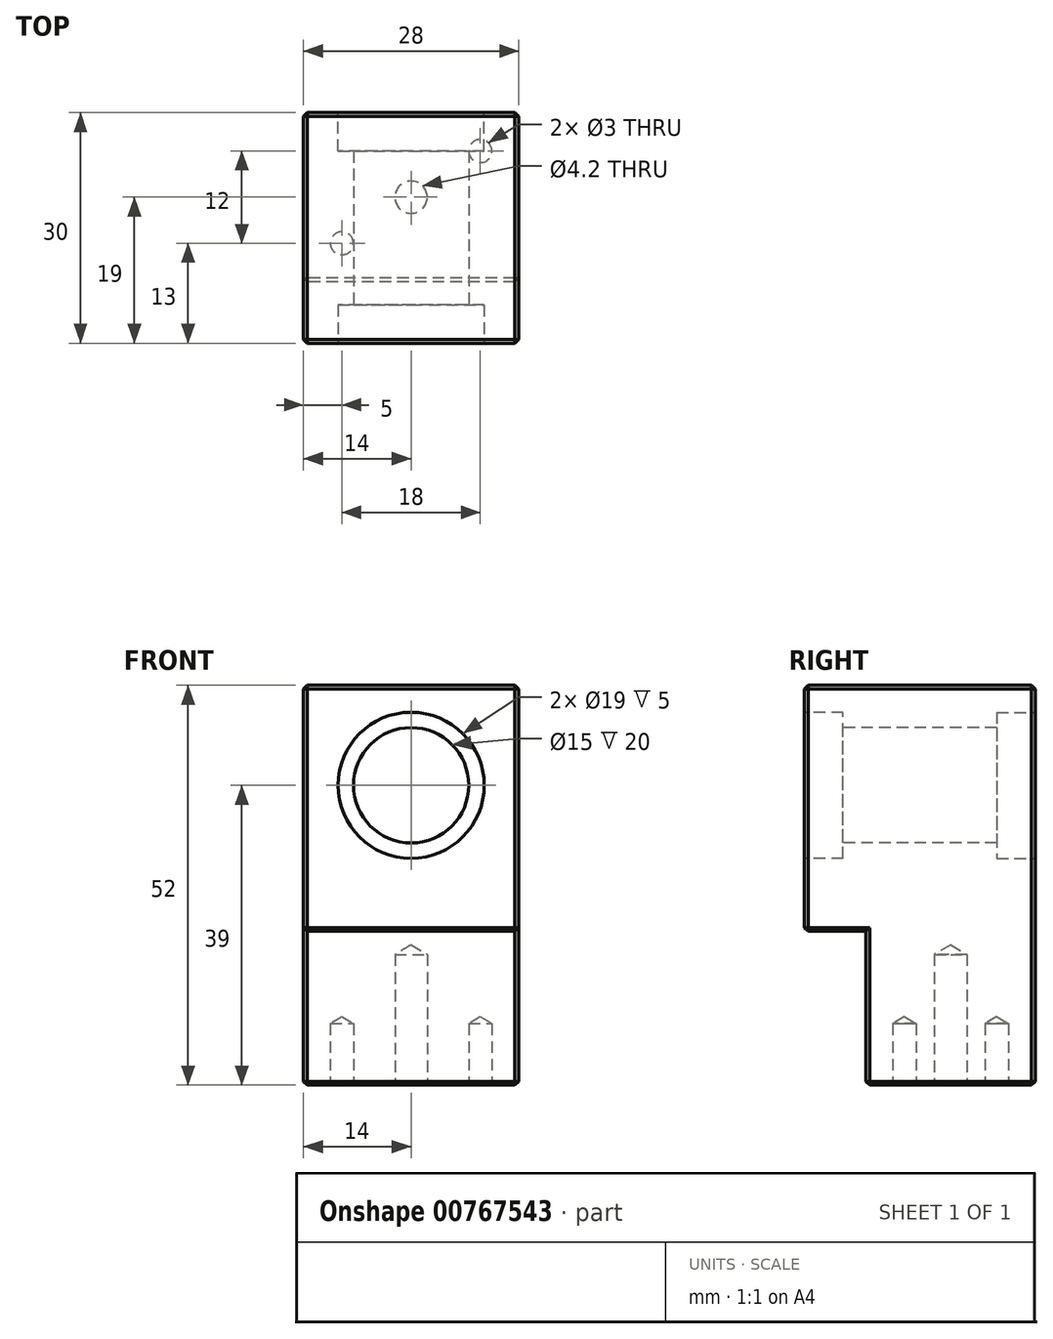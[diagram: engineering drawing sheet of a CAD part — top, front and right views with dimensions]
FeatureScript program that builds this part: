
annotation { "Feature Type Name" : "Feature", "Feature Type Description" : "" }
export const myFeature = defineFeature(function(context is Context, id is Id, definition is map)
    precondition{}
    {
        {
            var Q0;
            Q0=qCreatedBy(makeId("Right.planeOp"),FACE);
            var sketch = newSketch(context, id + "F0", { "sketchPlane" : qUnion([Q0])});
            skLineSegment(sketch, "E0", {"start": v(0, 0) * mm, "end": v(0, 20) * mm});
            skLineSegment(sketch, "E1", {"start": v(0, 20) * mm, "end": v(-8, 20) * mm});
            skLineSegment(sketch, "E2", {"start": v(-8, 20) * mm, "end": v(-8, 52) * mm});
            skLineSegment(sketch, "E3", {"start": v(-8, 52) * mm, "end": v(22, 52) * mm});
            skLineSegment(sketch, "E4", {"start": v(22, 52) * mm, "end": v(22, 0) * mm});
            skLineSegment(sketch, "E5", {"start": v(22, 0) * mm, "end": v(0, 0) * mm});
            skSolve(sketch);
        }
        {
            var Q0;
            Q0 = qSketchRegion(id + "F0", true);
            extrude(context, id + "F1", {"entities" : qUnion([Q0]), "endBound" : BoundingType.SYMMETRIC, "depth" : 28 * mm, "offsetDistance" : 25 * mm});
        }
        {
            var Q0;
            Q0=makeQuery(id+"F1.opExtrude","CAP_FACE",FACE,{"disambiguationData":[OSD([sQuery(id+"F0.wireOp",EDGE,"E0"),sQuery(id+"F0.wireOp",EDGE,"E1"),sQuery(id+"F0.wireOp",EDGE,"E2"),sQuery(id+"F0.wireOp",EDGE,"E3"),sQuery(id+"F0.wireOp",EDGE,"E4"),sQuery(id+"F0.wireOp",EDGE,"E5")])],"isStart":false});
            var Q1;
            Q1=makeQuery(id+"F1.opExtrude","CAP_FACE",FACE,{"disambiguationData":[OSD([sQuery(id+"F0.wireOp",EDGE,"E0"),sQuery(id+"F0.wireOp",EDGE,"E1"),sQuery(id+"F0.wireOp",EDGE,"E2"),sQuery(id+"F0.wireOp",EDGE,"E3"),sQuery(id+"F0.wireOp",EDGE,"E4"),sQuery(id+"F0.wireOp",EDGE,"E5")])],"isStart":true});
            var Q2;
            Q2=makeQuery(id+"F1.opExtrude","SWEPT_FACE",FACE,{"disambiguationData":[OSD([sQuery(id+"F0.wireOp",EDGE,"E5")])]});
            var Q3;
            Q3=makeQuery(id+"F1.opExtrude","SWEPT_FACE",FACE,{"disambiguationData":[OSD([sQuery(id+"F0.wireOp",EDGE,"E3")])]});
            var Q4;
            Q4=makeQuery(id+"F1.opExtrude","SWEPT_FACE",FACE,{"disambiguationData":[OSD([sQuery(id+"F0.wireOp",EDGE,"E2")])]});
            chamfer(context, id + "F2", {"entities" : qUnion([Q0, Q1, Q2, Q3, Q4]), "width" : 0.5 * mm, "tangentPropagation" : true});
        }
        {
            var Q0;
            Q0=makeQuery(id+"F1.opExtrude","SWEPT_FACE",FACE,{"disambiguationData":[OSD([sQuery(id+"F0.wireOp",EDGE,"E2")])]});
            var sketch = newSketch(context, id + "F3", { "sketchPlane" : qUnion([Q0])});
            skPoint(sketch, "E6", {"position": v(0, 39) * mm});
            skSolve(sketch);
        }
        {
            var Q0;
            Q0=sQuery(id+"F3.wireOp",VERTEX,"E6");
            var Q1;
            Q1=makeQuery(id+"F1.opExtrude","SWEPT_BODY",BODY,{"disambiguationData":[OSD([sQuery(id+"F0.wireOp",EDGE,"E0"),sQuery(id+"F0.wireOp",EDGE,"E1"),sQuery(id+"F0.wireOp",EDGE,"E2"),sQuery(id+"F0.wireOp",EDGE,"E3"),sQuery(id+"F0.wireOp",EDGE,"E4"),sQuery(id+"F0.wireOp",EDGE,"E5")])]});
            hole(context, id + "F4", {"style" : HoleStyle.C_BORE, "endStyle" : HoleEndStyle.THROUGH, "holeDiameter" : 15 * mm, "cBoreDiameter" : 19 * mm, "cBoreDepth" : 5 * mm, "majorDiameter" : 5 * mm, "tappedDepth" : 13.8 * mm, "tapClearance" : 4, "startFromSketch" : true, "locations" : qUnion([Q0]), "scope" : qUnion([Q1])});
        }
        {
            var Q0;
            Q0=makeQuery(id+"F1.opExtrude","SWEPT_FACE",FACE,{"disambiguationData":[OSD([sQuery(id+"F0.wireOp",EDGE,"E4")])]});
            var sketch = newSketch(context, id + "F5", { "sketchPlane" : qUnion([Q0])});
            skPoint(sketch, "E7.0", {"position": v(0, 39) * mm});
            skSolve(sketch);
        }
        {
            var Q0;
            Q0=sQuery(id+"F5.wireOp",VERTEX,"E7.0");
            var Q1;
            Q1=makeQuery(id+"F1.opExtrude","SWEPT_BODY",BODY,{"disambiguationData":[OSD([sQuery(id+"F0.wireOp",EDGE,"E0"),sQuery(id+"F0.wireOp",EDGE,"E1"),sQuery(id+"F0.wireOp",EDGE,"E2"),sQuery(id+"F0.wireOp",EDGE,"E3"),sQuery(id+"F0.wireOp",EDGE,"E4"),sQuery(id+"F0.wireOp",EDGE,"E5")])]});
            hole(context, id + "F6", {"style" : HoleStyle.C_BORE, "endStyle" : HoleEndStyle.BLIND, "holeDiameter" : 15 * mm, "cBoreDiameter" : 19 * mm, "cBoreDepth" : 5 * mm, "majorDiameter" : 5 * mm, "holeDepth" : 17 * mm, "tappedDepth" : 13.8 * mm, "tapClearance" : 4, "startFromSketch" : true, "locations" : qUnion([Q0]), "scope" : qUnion([Q1])});
        }
        {
            var Q0;
            Q0=qCreatedBy(makeId("Top.planeOp"),FACE);
            var sketch = newSketch(context, id + "F7", { "sketchPlane" : qUnion([Q0])});
            skPoint(sketch, "E8", {"position": v(0, 11) * mm});
            skPoint(sketch, "E9", {"position": v(-9, 5) * mm});
            skPoint(sketch, "E10", {"position": v(9, 17) * mm});
            skSolve(sketch);
        }
        {
            var Q0;
            Q0=sQuery(id+"F7.wireOp",VERTEX,"E8");
            var Q1;
            Q1=makeQuery(id+"F1.opExtrude","SWEPT_BODY",BODY,{"disambiguationData":[OSD([sQuery(id+"F0.wireOp",EDGE,"E0"),sQuery(id+"F0.wireOp",EDGE,"E1"),sQuery(id+"F0.wireOp",EDGE,"E2"),sQuery(id+"F0.wireOp",EDGE,"E3"),sQuery(id+"F0.wireOp",EDGE,"E4"),sQuery(id+"F0.wireOp",EDGE,"E5")])]});
            hole(context, id + "F8", {"style" : HoleStyle.SIMPLE, "endStyle" : HoleEndStyle.BLIND, "oppositeDirection" : true, "standardTappedOrClearance" : lookupTablePath({ "standard" : "ISO", "engagement" : "75%", "pitch" : "0.8 mm", "size" : "M5", "type" : "Tapped" }), "standardBlindInLast" : lookupTablePath({ "standard" : "ISO", "engagement" : "75%", "pitch" : "0.8 mm", "size" : "M5", "type" : "Tapped" }), "holeDiameter" : 4.2 * mm, "majorDiameter" : 5 * mm, "showTappedDepth" : true, "holeDepth" : 17 * mm, "tappedDepth" : 13.8 * mm, "tapClearance" : 4, "startFromSketch" : true, "locations" : qUnion([Q0]), "scope" : qUnion([Q1])});
        }
        {
            var Q0;
            Q0=sQuery(id+"F7.wireOp",VERTEX,"E9");
            var Q1;
            Q1=sQuery(id+"F7.wireOp",VERTEX,"E10");
            var Q2;
            Q2=makeQuery(id+"F1.opExtrude","SWEPT_BODY",BODY,{"disambiguationData":[OSD([sQuery(id+"F0.wireOp",EDGE,"E0"),sQuery(id+"F0.wireOp",EDGE,"E1"),sQuery(id+"F0.wireOp",EDGE,"E2"),sQuery(id+"F0.wireOp",EDGE,"E3"),sQuery(id+"F0.wireOp",EDGE,"E4"),sQuery(id+"F0.wireOp",EDGE,"E5")])]});
            hole(context, id + "F9", {"style" : HoleStyle.SIMPLE, "endStyle" : HoleEndStyle.BLIND, "oppositeDirection" : true, "holeDiameter" : 3 * mm, "majorDiameter" : 5 * mm, "holeDepth" : 8 * mm, "tappedDepth" : 13.8 * mm, "tapClearance" : 4, "startFromSketch" : true, "locations" : qUnion([Q0, Q1]), "scope" : qUnion([Q2])});
        }
    });
